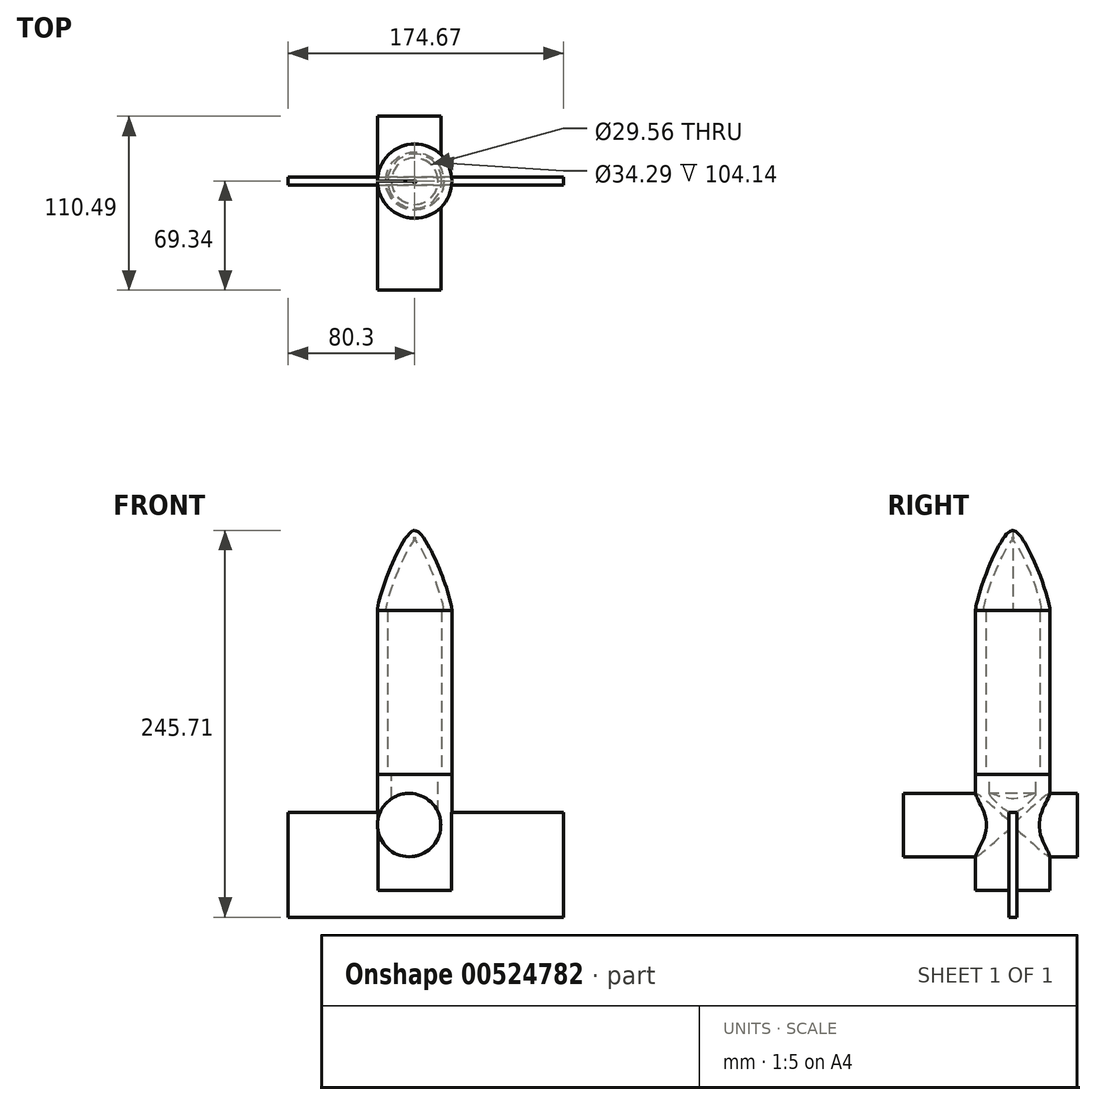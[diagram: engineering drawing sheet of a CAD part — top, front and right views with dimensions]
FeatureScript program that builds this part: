
annotation { "Feature Type Name" : "Feature", "Feature Type Description" : "" }
export const myFeature = defineFeature(function(context is Context, id is Id, definition is map)
    precondition{}
    {
        {
            var Q0;
            Q0=qCreatedBy(makeId("Top.planeOp"),FACE);
            var sketch = newSketch(context, id + "F0", { "sketchPlane" : qUnion([Q0])});
            skCircle(sketch, "E0", {"center": v(0, 0) * mm, "radius": 23.6 * mm});
            skCircle(sketch, "E1", {"center": v(0, 0) * mm, "radius": 17.14 * mm});
            skSolve(sketch);
        }
        {
            var Q0;
            Q0 = qSketchRegion(id + "F0", true);
            extrude(context, id + "F1", {"entities" : qUnion([Q0]), "depth" : 104.14 * mm, "offsetDistance" : 25.4 * mm});
        }
        {
            var Q0;
            Q0=makeQuery(id+"F1.opExtrude","CAP_FACE",FACE,{"disambiguationData":[OSD([sQuery(id+"F0.wireOp",EDGE,"E0"),sQuery(id+"F0.wireOp",EDGE,"E1")])],"isStart":true});
            var sketch = newSketch(context, id + "F2", { "sketchPlane" : qUnion([Q0])});
            skCircle(sketch, "E2.0", {"center": v(0, 0) * mm, "radius": 23.6 * mm});
            skSolve(sketch);
        }
        {
            var Q0;
            Q0 = qSketchRegion(id + "F2", true);
            extrude(context, id + "F3", {"entities" : qUnion([Q0]), "depth" : 73.66 * mm, "offsetDistance" : 25.4 * mm});
        }
        {
            var Q0;
            Q0=qCreatedBy(makeId("Front.planeOp"),FACE);
            var sketch = newSketch(context, id + "F4", { "sketchPlane" : qUnion([Q0])});
            skLineSegment(sketch, "E3.bottom", {"start": v(-80.3, -24.36) * mm, "end": v(94.37, -24.36) * mm});
            skLineSegment(sketch, "E3.top", {"start": v(-80.3, -90.77) * mm, "end": v(94.37, -90.77) * mm});
            skLineSegment(sketch, "E3.left", {"start": v(-80.3, -24.36) * mm, "end": v(-80.3, -90.77) * mm});
            skLineSegment(sketch, "E3.right", {"start": v(94.37, -24.36) * mm, "end": v(94.37, -90.77) * mm});
            skSolve(sketch);
        }
        {
            var Q0;
            Q0=makeQuery(id+"F1.opExtrude","CAP_FACE",FACE,{"disambiguationData":[OSD([sQuery(id+"F0.wireOp",EDGE,"E0"),sQuery(id+"F0.wireOp",EDGE,"E1")])],"isStart":false});
            cPlane(context, id + "F5", {"entities" : qUnion([Q0]), "cplaneType" : CPlaneType.OFFSET, "offset" : 50.8 * mm, "width" : 152.4 * mm, "height" : 152.4 * mm});
        }
        {
            var Q0;
            Q0 = qSketchRegion(id + "F4", true);
            extrude(context, id + "F6", {"entities" : qUnion([Q0]), "operationType" : NewBodyOperationType.ADD, "depth" : 2.54 * mm, "offsetDistance" : 25.4 * mm, "hasSecondDirection" : true, "secondDirectionOppositeDirection" : true, "secondDirectionDepth" : 2.54 * mm});
        }
        {
            var Q0;
            Q0=qCreatedBy(id+"F5.planeOp",FACE);
            var sketch = newSketch(context, id + "F7", { "sketchPlane" : qUnion([Q0])});
            skPoint(sketch, "E4", {"position": v(0, 0) * mm});
            skSolve(sketch);
        }
        {
            var Q0;
            Q0=makeQuery(id+"F3.opExtrude","CAP_FACE",FACE,{"disambiguationData":[OSD([sQuery(id+"F2.wireOp",EDGE,"E2.0")])],"isStart":true});
            var sketch = newSketch(context, id + "F8", { "sketchPlane" : qUnion([Q0])});
            skCircle(sketch, "E5", {"center": v(0, 0) * mm, "radius": 14.78 * mm});
            skSolve(sketch);
        }
        {
            var Q0;
            Q0 = qSketchRegion(id + "F8", true);
            extrude(context, id + "F9", {"entities" : qUnion([Q0]), "operationType" : NewBodyOperationType.REMOVE, "oppositeDirection" : true, "depth" : 25.4 * mm, "offsetDistance" : 25.4 * mm});
        }
        {
            var Q0;
            Q0=makeQuery(id+"F1.opExtrude","CAP_FACE",FACE,{"disambiguationData":[OSD([sQuery(id+"F0.wireOp",EDGE,"E0"),sQuery(id+"F0.wireOp",EDGE,"E1")])],"isStart":false});
            var sketch = newSketch(context, id + "F10", { "sketchPlane" : qUnion([Q0])});
            skCircle(sketch, "E6.0", {"center": v(0, 0) * mm, "radius": 23.6 * mm});
            skSolve(sketch);
        }
        {
            var Q0;
            Q0=makeQuery(id+"F6.opExtrude","CAP_FACE",FACE,{"disambiguationData":[OSD([sQuery(id+"F4.wireOp",EDGE,"E3.bottom"),sQuery(id+"F4.wireOp",EDGE,"E3.top"),sQuery(id+"F4.wireOp",EDGE,"E3.left"),sQuery(id+"F4.wireOp",EDGE,"E3.right")])],"isStart":true});
            var sketch = newSketch(context, id + "F11", { "sketchPlane" : qUnion([Q0])});
            skCircle(sketch, "E7", {"center": v(3.56, -32.25) * mm, "radius": 20.1 * mm});
            skSolve(sketch);
        }
        {
            var Q0;
            Q0=sQuery(id+"F7.wireOp",VERTEX,"E4");
            var Q1;
            Q1 = qSketchRegion(id + "F10", true);
            loft(context, id + "F12", {"startCondition" : LoftEndDerivativeType.TANGENT_TO_PROFILE, "startMagnitude" : 1, "endCondition" : LoftEndDerivativeType.NORMAL_TO_PROFILE, "endMagnitude" : 0.5, "sheetProfilesArray" : [{ "sheetProfileEntities" : qUnion([Q0]) }, { "sheetProfileEntities" : qUnion([Q1]) }]});
        }
        {
            var Q0;
            Q0 = qSketchRegion(id + "F11", true);
            extrude(context, id + "F13", {"entities" : qUnion([Q0]), "operationType" : NewBodyOperationType.ADD, "depth" : 38.6 * mm, "offsetDistance" : 25.4 * mm, "hasSecondDirection" : true, "secondDirectionOppositeDirection" : true, "secondDirectionDepth" : 71.88 * mm});
        }
        {
            var Q0;
            Q0=makeQuery(id+"F12.opLoft","CAP_FACE",FACE,{"disambiguationData":[OSD([makeQuery(id+"F10.imprint","IMPRINT",FACE,{"disambiguationData":[TD([[makeQuery(id+"F10.imprint","IMPRINT",EDGE,{"derivedFrom":makeQuery(id+"F1.opExtrude","CAP_EDGE",EDGE,{"disambiguationData":[OSD([sQuery(id+"F0.wireOp",EDGE,"E1")])],"isStart":false})}),1.0]])]})])],"isStart":true});
            shell(context, id + "F14", {"entities" : qUnion([Q0]), "thickness" : 5.08 * mm});
        }
    });
